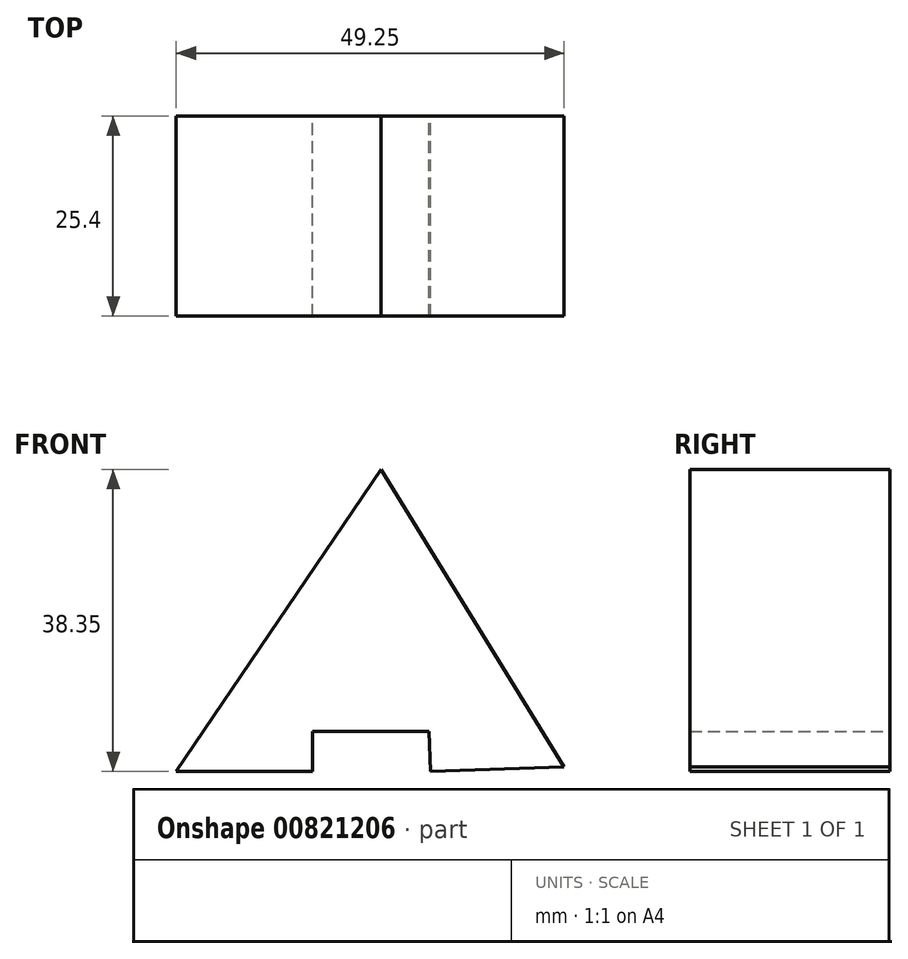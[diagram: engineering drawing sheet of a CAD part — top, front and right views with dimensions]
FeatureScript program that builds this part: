
annotation { "Feature Type Name" : "Feature", "Feature Type Description" : "" }
export const myFeature = defineFeature(function(context is Context, id is Id, definition is map)
    precondition{}
    {
        {
            var Q0;
            Q0=qCreatedBy(makeId("Front.planeOp"),FACE);
            var sketch = newSketch(context, id + "F0", { "sketchPlane" : qUnion([Q0])});
            skLineSegment(sketch, "E0", {"start": v(0, 55.38) * mm, "end": v(-25.99, 17.03) * mm});
            skLineSegment(sketch, "E1", {"start": v(0, 55.38) * mm, "end": v(23.26, 17.62) * mm});
            skLineSegment(sketch, "E2", {"start": v(-25.99, 17.03) * mm, "end": v(-8.66, 17.03) * mm});
            skLineSegment(sketch, "E3", {"start": v(23.26, 17.62) * mm, "end": v(6.33, 17.03) * mm});
            skLineSegment(sketch, "E4", {"start": v(-8.66, 17.03) * mm, "end": v(-8.66, 22.1) * mm});
            skLineSegment(sketch, "E5", {"start": v(-8.66, 22.1) * mm, "end": v(6.13, 22.1) * mm});
            skLineSegment(sketch, "E6", {"start": v(6.33, 17.03) * mm, "end": v(6.13, 22.1) * mm});
            skSolve(sketch);
        }
        {
            var Q0;
            Q0=makeQuery(id+"F0.imprint","IMPRINT",FACE,{"disambiguationData":[TD([[makeQuery(id+"F0.imprint","IMPRINT",EDGE,{"derivedFrom":sQuery(id+"F0.wireOp",EDGE,"E0")}),1.0]])]});
            extrude(context, id + "F1", {"entities" : qUnion([Q0]), "depth" : 25.4 * mm, "offsetDistance" : 25.4 * mm});
        }
    });
